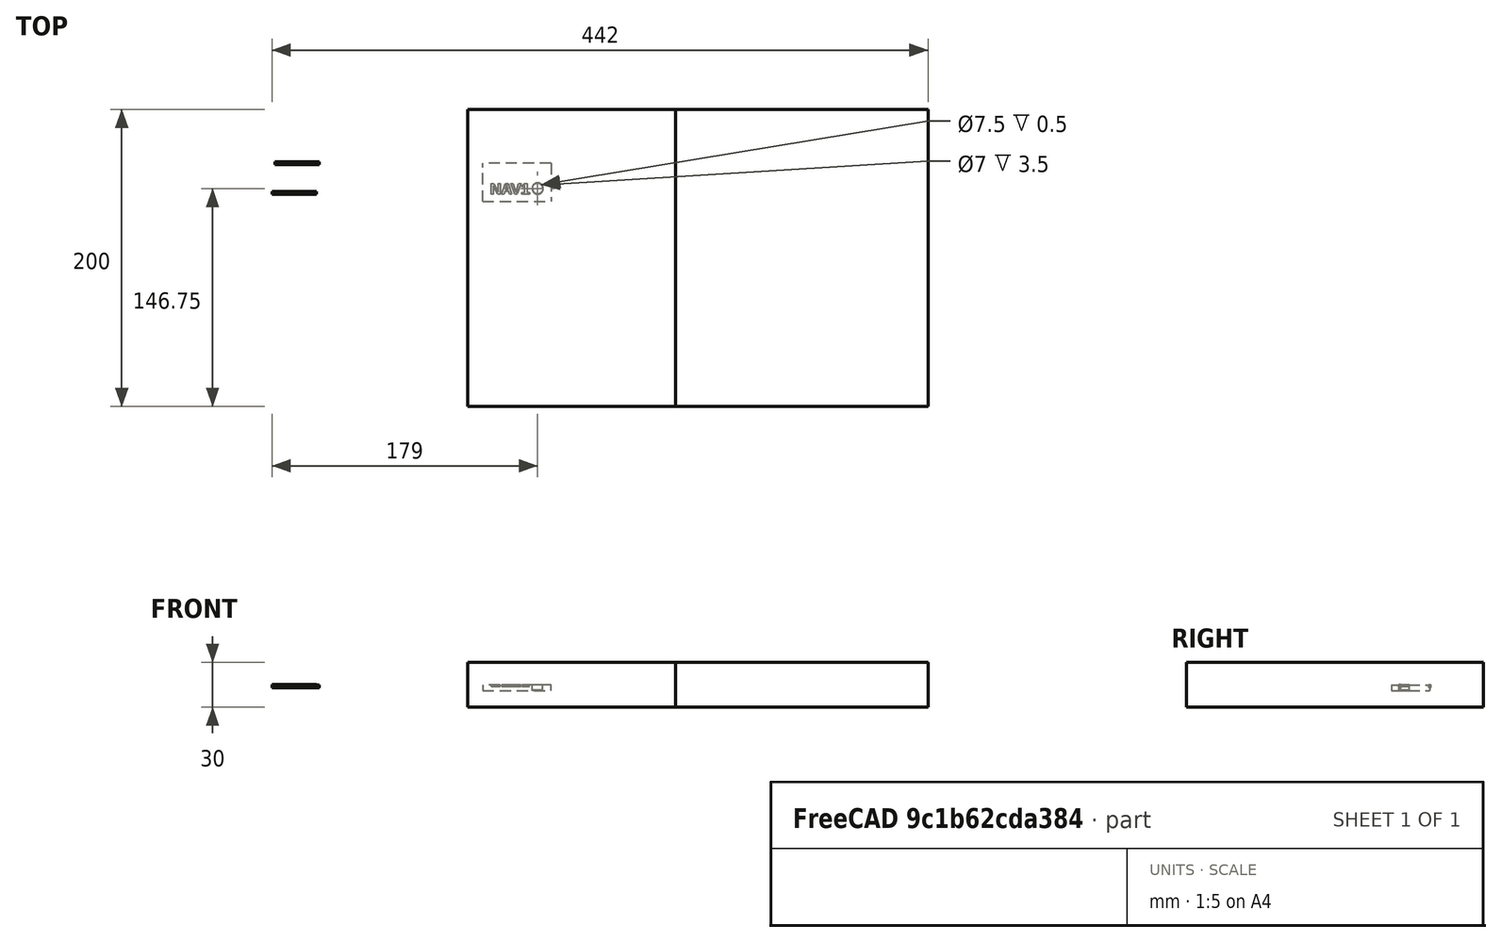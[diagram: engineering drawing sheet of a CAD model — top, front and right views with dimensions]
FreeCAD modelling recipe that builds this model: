
FCSTD DOCUMENT  (FreeCAD 0.17R13522 (Git))
Label: letras_led_1
License: CreativeCommons Attribution-ShareAlike
LicenseURL: http://creativecommons.org/licenses/by-sa/4.0/
objects: Part::Cut×35, Part::Feature×29, Part::Box×10, Part::Part2DObjectPython×7, Part::Fuse×7, Part::Cylinder×5, App::DocumentObjectGroup×3, Part::Extrusion×1
note: 94 computed .brp shape members not serialized (recipe doc carries the construction recipe); baked Part::Feature solids carry a one-line shape summary decoded from their .brp

FEATURE [Part::Part2DObjectPython] Line009  # Draft 2D object (typed FeaturePython)
  ChamferSize = 0
  Closed = false
  End = (270.847,20.2,0)
  FilletRadius = 0
  Length = 35.3471
  MakeFace = false
  Points = (2) [(235.5,20.2,0),(270.847,20.2,0)]
  Start = (235.5,20.2,0)
  Subdivisions = 0
FEATURE [Part::Part2DObjectPython] Circle001  # Draft 2D object (typed FeaturePython)
  FirstAngle = 0
  LastAngle = 0
  MakeFace = false
  Placement = pos=(259.67,20.2,0) rot=(0,0,1;0rad)
  Radius = 14
FEATURE [Part::Part2DObjectPython] Line014  # Draft 2D object (typed FeaturePython)
  ChamferSize = 0
  Closed = false
  End = (248.272,28.2144,0)
  FilletRadius = 0
  Length = 13.696
  MakeFace = false
  Placement = pos=(-10,0,-4) rot=(0,0,1;0rad)
  Points = (2) [(269.378,20.2,4),(258.272,28.2144,4)]
  Start = (259.378,20.2,0)
  Subdivisions = 0
FEATURE [Part::Part2DObjectPython] Line015  # Draft 2D object (typed FeaturePython)
  ChamferSize = 0
  Closed = false
  End = (254.876,33.263,0)
  FilletRadius = 0
  Length = 13.7518
  MakeFace = false
  Placement = pos=(-10,0,-4) rot=(0,0,1;0rad)
  Points = (2) [(269.174,20.2,4),(264.876,33.263,4)]
  Start = (259.174,20.2,0)
  Subdivisions = 0
FEATURE [Part::Part2DObjectPython] Line016  # Draft 2D object (typed FeaturePython)
  ChamferSize = 0
  Closed = false
  End = (263.227,33.6931,0)
  FilletRadius = 0
  Length = 14.1488
  MakeFace = false
  Placement = pos=(-10,0,-4) rot=(0,0,1;0rad)
  Points = (2) [(268.97,20.2,4),(273.227,33.6931,4)]
  Start = (258.97,20.2,0)
  Subdivisions = 0
FEATURE [Part::Part2DObjectPython] Line017  # Draft 2D object (typed FeaturePython)
  ChamferSize = 0
  Closed = false
  End = (270.612,28.9289,0)
  FilletRadius = 0
  Length = 14.5511
  MakeFace = false
  Placement = pos=(-10,0,-4) rot=(0,0,1;0rad)
  Points = (2) [(268.97,20.2,4),(280.612,28.9289,4)]
  Start = (258.97,20.2,0)
  Subdivisions = 0
FEATURE [App::DocumentObjectGroup] Construction
  Group = -> [Line009,Circle001,Line014,Line015,Line016,Line017]
FEATURE [Part::Box] Box001  label="Cube"
  AttacherType = Attacher::AttachEngine3D
  Height = 3
  Length = 6
  Placement = pos=(39,81,-108) rot=(0,0,1;0rad)
  Width = 6
FEATURE [Part::Feature] Fusion008001001061001  label="panel_siplays_encoders_dobles_y_spacers"
  Placement = pos=(0,0,-105) rot=(0,0,1;0rad)
  shape: bbox 280 x 210 x 10 mm, 411 faces (baked)
FEATURE [Part::Feature] Fusion003002001  label="el perforador001"
  Placement = pos=(48,115,-108) rot=(0,1,0;3.14159rad)
  shape: bbox 22 x 12 x 18 mm, 19 faces (baked)
FEATURE [Part::Feature] Fusion003002001001  label="el perforador002"
  Placement = pos=(87.5,115,-108) rot=(0,1,0;3.14159rad)
  shape: bbox 22 x 12 x 18 mm, 19 faces (baked)
FEATURE [Part::Cut] Cut001001001002003001008002002004
  Base = -> Fusion008001001061001
  Refine = true
  Tool = -> Fusion003002001
FEATURE [Part::Feature] Fusion003002001001001  label="el perforador003"
  Placement = pos=(127,115,-108) rot=(0,1,0;3.14159rad)
  shape: bbox 22 x 12 x 18 mm, 19 faces (baked)
FEATURE [Part::Cut] Cut001001001002003001008002002005
  Base = -> Cut001001001002003001008002002004
  Refine = true
  Tool = -> Fusion003002001001
FEATURE [Part::Feature] Fusion003002001001001001  label="el perforador004"
  Placement = pos=(166.5,115,-108) rot=(0,1,0;3.14159rad)
  shape: bbox 22 x 12 x 18 mm, 19 faces (baked)
FEATURE [Part::Feature] Fusion003002001001001001001  label="el perforador005"
  Placement = pos=(206,115,-108) rot=(0,1,0;3.14159rad)
  shape: bbox 22 x 12 x 18 mm, 19 faces (baked)
FEATURE [Part::Cut] Cut001001001002003001008002002006
  Base = -> Cut001001001002003001008002002005
  Refine = true
  Tool = -> Fusion003002001001001001
FEATURE [Part::Cut] Cut001001001002003001008002002007
  Base = -> Cut001001001002003001008002002006
  Refine = true
  Tool = -> Fusion003002001001001001001
FEATURE [Part::Feature] Fusion003002001001001001002001001  label="el perforador008"
  Placement = pos=(127,40,-108) rot=(0,1,0;3.14159rad)
  shape: bbox 22 x 12 x 18 mm, 19 faces (baked)
FEATURE [Part::Feature] Fusion003002001001001001002001002  label="el perforador009"
  Placement = pos=(127,80.5,-108) rot=(0,1,0;3.14159rad)
  shape: bbox 22 x 12 x 18 mm, 19 faces (baked)
FEATURE [Part::Feature] Fusion003002001001001001002001  label="el perforador007"
  Placement = pos=(127,55,-108) rot=(0,1,0;3.14159rad)
  shape: bbox 22 x 12 x 18 mm, 19 faces (baked)
FEATURE [Part::Feature] Fusion003002001001001001002  label="el perforador006"
  Placement = pos=(127,95.5,-108) rot=(0,1,0;3.14159rad)
  shape: bbox 22 x 12 x 18 mm, 19 faces (baked)
FEATURE [Part::Cut] Cut001001001002003001008002002008
  Base = -> Cut001001001002003001008002002007
  Refine = true
  Tool = -> Fusion003002001001001
FEATURE [Part::Cut] Cut001001001002003001008002002009
  Base = -> Cut001001001002003001008002002008
  Refine = true
  Tool = -> Fusion003002001001001001002
FEATURE [Part::Cut] Cut001001001002003001008002002010
  Base = -> Cut001001001002003001008002002009
  Refine = true
  Tool = -> Fusion003002001001001001002001
FEATURE [Part::Box] Box001001002002002001003001001004001001001001001001002  label="Cube034"
  AttacherType = Attacher::AttachEngine3D
  Height = 4
  Length = 32
  Placement = pos=(200,15,-108) rot=(0,0,1;0rad)
  Width = 10
FEATURE [Part::Fuse] Fusion003002001001001001002001003
  Base = -> Cut001001001002003001008002002010
  Refine = true
  Tool = -> Box001001002002002001003001001004001001001001001001002
FEATURE [Part::Fuse] Fusion003002001001001001002001004
  Base = -> Box001001002002002001003001001004001001001001001001002
  Refine = true
  Tool = -> Fusion003002001001001001002001003
FEATURE [Part::Fuse] Fusion003002001001001001002001005
  Refine = true
  Tool = -> Fusion003002001001001001002001004
FEATURE [Part::Fuse] Fusion003002001001001001002001006
  Base = -> Box001
  Refine = true
  Tool = -> Fusion003002001001001001002001005
FEATURE [Part::Feature] Fusion003002001001001001002001002001  label="el perforador010"
  Placement = pos=(47,80.5,-108) rot=(0,1,0;3.14159rad)
  shape: bbox 22 x 12 x 18 mm, 19 faces (baked)
FEATURE [Part::Feature] Fusion003002001001001001002001002002  label="el perforador011"
  Placement = pos=(87,80.5,-108) rot=(0,1,0;3.14159rad)
  shape: bbox 22 x 12 x 18 mm, 19 faces (baked)
FEATURE [Part::Feature] Fusion003002001001001001002001001001  label="el perforador012"
  Placement = pos=(87,40,-108) rot=(0,1,0;3.14159rad)
  shape: bbox 22 x 12 x 18 mm, 19 faces (baked)
FEATURE [Part::Feature] Fusion003002001001001001002001001001001  label="el perforador013"
  Placement = pos=(47,40,-108) rot=(0,1,0;3.14159rad)
  shape: bbox 22 x 12 x 18 mm, 19 faces (baked)
FEATURE [Part::Cut] Cut001001001002003001008002002011
  Base = -> Fusion003002001001001001002001006
  Refine = true
  Tool = -> Fusion003002001001001001002001002
FEATURE [Part::Cut] Cut001001001002003001008002002012
  Base = -> Cut001001001002003001008002002011
  Refine = true
  Tool = -> Fusion003002001001001001002001002002
FEATURE [Part::Cut] Cut001001001002003001008002002013
  Base = -> Cut001001001002003001008002002012
  Refine = true
  Tool = -> Fusion003002001001001001002001002001
FEATURE [Part::Cut] Cut001001001002003001008002002014
  Base = -> Cut001001001002003001008002002013
  Refine = true
  Tool = -> Fusion003002001001001001002001001001001
FEATURE [Part::Feature] Fusion003002001001001001002001001001002  label="el perforador014"
  Placement = pos=(220,8,-108) rot=(0.707107,0.707107,0;3.14159rad)
  shape: bbox 12 x 22 x 18 mm, 19 faces (baked)
FEATURE [Part::Cut] Cut001001001002003001008002002015
  Base = -> Cut001001001002003001008002002014
  Refine = true
  Tool = -> Fusion003002001001001001002001001001
FEATURE [Part::Cut] Cut001001001002003001008002002016
  Base = -> Cut001001001002003001008002002015
  Refine = true
  Tool = -> Fusion003002001001001001002001001
FEATURE [Part::Cut] Cut001001001002003001008002002017  label="base solo faltan los leds"
  Base = -> Cut001001001002003001008002002016
  Refine = true
  Tool = -> Fusion003002001001001001002001001001002
FEATURE [Part::Feature] Fusion001001  label="perforador led 3 mm001 rojo com2"
  Placement = pos=(24,43,-108) rot=(0,1,0;3.14159rad)
  shape: bbox 6 x 6 x 10 mm, 13 faces (baked)
FEATURE [Part::Feature] Fusion003002001001001001002001001001003  label="perforador led 3 mm002 rojo nav2"
  Placement = pos=(61,43,-108) rot=(0,1,0;3.14159rad)
  shape: bbox 6 x 6 x 10 mm, 13 faces (baked)
FEATURE [Part::Feature] Fusion003002001001001001002001001001004  label="perforador led 3 mm002 rojo adf2"
  Placement = pos=(101,43,-108) rot=(0,1,0;3.14159rad)
  shape: bbox 6 x 6 x 10 mm, 13 faces (baked)
FEATURE [Part::Feature] Fusion003002001001001001002001001001005  label="perforador led 3 mm001 rojo com1"
  Placement = pos=(24,83.5,-108) rot=(0,1,0;3.14159rad)
  shape: bbox 6 x 6 x 10 mm, 13 faces (baked)
FEATURE [Part::Feature] Fusion003002001001001001002001001001006  label="perforador led 3 mm002 rojo nav1"
  Placement = pos=(61,83.5,-108) rot=(0,1,0;3.14159rad)
  shape: bbox 6 x 6 x 10 mm, 13 faces (baked)
FEATURE [Part::Feature] Fusion003002001001001001002001001001007  label="perforador led 3 mm002 rojo adf1"
  Placement = pos=(101,83.5,-108) rot=(0,1,0;3.14159rad)
  shape: bbox 6 x 6 x 10 mm, 13 faces (baked)
FEATURE [Part::Cut] Cut
  Base = -> Cut001001001002003001008002002017
  Refine = true
  Tool = -> Fusion003002001001001001002001001001005
FEATURE [Part::Cut] Cut001001001002003001008002002018
  Base = -> Cut
  Refine = true
  Tool = -> Fusion003002001001001001002001001001006
FEATURE [Part::Cut] Cut001001001002003001008002002019
  Base = -> Cut001001001002003001008002002018
  Refine = true
  Tool = -> Fusion003002001001001001002001001001007
FEATURE [Part::Cut] Cut001001001002003001008002002020
  Base = -> Cut001001001002003001008002002019
  Refine = true
  Tool = -> Fusion003002001001001001002001001001004
FEATURE [Part::Cut] Cut001001001002003001008002002021
  Base = -> Cut001001001002003001008002002020
  Refine = true
  Tool = -> Fusion003002001001001001002001001001003
FEATURE [Part::Cut] Cut001001001002003001008002002022
  Base = -> Cut001001001002003001008002002021
  Refine = true
  Tool = -> Fusion001001
FEATURE [Part::Feature] Fusion003002001001001001002001001001008  label="perforador led 5 mm sound marker"
  Placement = pos=(40.75,133,-108) rot=(0,1,0;3.14159rad)
  shape: bbox 7.5 x 7.5 x 10 mm, 13 faces (baked)
FEATURE [Part::Feature] Fusion003002001001001001002001001001009  label="perforador led 5 mm sound com1"
  Placement = pos=(80.25,133,-108) rot=(0,1,0;3.14159rad)
  shape: bbox 7.5 x 7.5 x 10 mm, 13 faces (baked)
FEATURE [Part::Feature] Fusion003002001001001001002001001001010  label="perforador led 5 mm sound nav1"
  Placement = pos=(119.75,133,-108) rot=(0,1,0;3.14159rad)
  shape: bbox 7.5 x 7.5 x 10 mm, 13 faces (baked)
FEATURE [Part::Feature] Fusion003002001001001001002001001001011  label="perforador led 5 mm sound dme"
  Placement = pos=(159.25,133,-108) rot=(0,1,0;3.14159rad)
  shape: bbox 7.5 x 7.5 x 10 mm, 13 faces (baked)
FEATURE [Part::Feature] Fusion003002001001001001002001001001012  label="perforador led 5 mm sound adf1"
  Placement = pos=(198.75,133,-108) rot=(0,1,0;3.14159rad)
  shape: bbox 7.5 x 7.5 x 10 mm, 13 faces (baked)
FEATURE [Part::Feature] Fusion003002001001001001002001001001013  label="perforador led 5 mm ON/OFF"
  Placement = pos=(263.5,133,-108) rot=(0,1,0;3.14159rad)
  shape: bbox 7.5 x 7.5 x 10 mm, 13 faces (baked)
FEATURE [Part::Cut] Cut001001001002003001008002002023
  Base = -> Cut001001001002003001008002002022
  Refine = true
  Tool = -> Fusion003002001001001001002001001001013
FEATURE [Part::Cut] Cut001001001002003001008002002024
  Base = -> Cut001001001002003001008002002023
  Refine = true
  Tool = -> Fusion003002001001001001002001001001012
FEATURE [Part::Cut] Cut001001001002003001008002002025
  Base = -> Cut001001001002003001008002002024
  Refine = true
  Tool = -> Fusion003002001001001001002001001001011
FEATURE [Part::Cut] Cut001001001002003001008002002026
  Base = -> Cut001001001002003001008002002025
  Refine = true
  Tool = -> Fusion003002001001001001002001001001010
FEATURE [Part::Cut] Cut001001001002003001008002002027
  Base = -> Cut001001001002003001008002002026
  Refine = true
  Tool = -> Fusion003002001001001001002001001001009
FEATURE [Part::Cut] Cut001001001002003001008002002028
  Base = -> Cut001001001002003001008002002027
  Refine = true
  Tool = -> Fusion003002001001001001002001001001008
FEATURE [Part::Box] Box  label="Cube035"
  AttacherType = Attacher::AttachEngine3D
  Height = 10
  Length = 300
  Placement = pos=(-8,153.85,-111) rot=(0,0,1;0rad)
  Width = 120
FEATURE [Part::Cut] Cut001001001002003001008002002029  label="panel sin letras"
  Base = -> Cut001001001002003001008002002028
  Refine = true
  Tool = -> Box
FEATURE [Part::Box] Box001001002002002001003001001004001001001001001001003  label="cortador saca parte izquierda"
  AttacherType = Attacher::AttachEngine3D
  Height = 30
  Length = 140
  Placement = pos=(-10,-10,-119) rot=(0,0,1;0rad)
  Width = 200
FEATURE [Part::Box] Box001001002002002001003001001004001001001001001001004  label="cortador saca parte derecha"
  AttacherType = Attacher::AttachEngine3D
  Height = 30
  Length = 170
  Placement = pos=(130,-10,-119) rot=(0,0,1;0rad)
  Width = 200
FEATURE [Part::Cylinder] Cylinder  label="clavija agujereadora1_1"
  Angle = 360
  AttacherType = Attacher::AttachEngine3D
  Height = 30
  Placement = pos=(115,111.85,-106) rot=(0,1,0;1.5708rad)
  Radius = 1.05
FEATURE [Part::Cylinder] Cylinder001  label="clavija agujereadora2_1"
  Angle = 360
  AttacherType = Attacher::AttachEngine3D
  Height = 30
  Placement = pos=(115,37.85,-106) rot=(0,1,0;1.5708rad)
  Radius = 1.05
FEATURE [Part::Cylinder] Cylinder002  label="clavija empalmadora1"
  Angle = 360
  AttacherType = Attacher::AttachEngine3D
  Height = 29.8
  Placement = pos=(-140,153.85,-105) rot=(0,1,0;1.5708rad)
  Radius = 1
FEATURE [Part::Cut] Cut001001001002003001008002002030
  Base = -> Cut001001001002003001008002002029
  Refine = true
  Tool = -> Cylinder
FEATURE [Part::Cut] Cut001001001002003001008002002031  label="panel sin letras con agujeros clavijas"
  Base = -> Cut001001001002003001008002002030
  Refine = true
  Tool = -> Cylinder001
FEATURE [App::DocumentObjectGroup] Group  label="cortadores principales"
  Group = -> [Box001001002002002001003001001004001001001001001001003,Box001001002002002001003001001004001001001001001001004]
FEATURE [Part::Cylinder] Cylinder003  label="clavija hace agujero"
  Angle = 360
  AttacherType = Attacher::AttachEngine3D
  Height = 30
  Placement = pos=(-142,133.85,-105) rot=(0,1,0;1.5708rad)
  Radius = 1.05
FEATURE [App::DocumentObjectGroup] Group001  label="clavijas"
  Group = -> [Cylinder003,Cylinder002]
FEATURE [Part::Box] Box001001002002002001003001001004001001001001001001006  label="fleje abajo"
  AttacherType = Attacher::AttachEngine3D
  Height = 4
  Length = 280
  Placement = pos=(0,-4,-108) rot=(0,0,1;0rad)
  Width = 4
FEATURE [Part::Fuse] Fusion
  Base = -> Cut001001001002003001008002002031
  Refine = true
  Tool = -> Box001001002002002001003001001004001001001001001001006
FEATURE [Part::Feature] Cylinder002001  label="clavija empalmadora une frente base"
  Placement = pos=(30,-2,-134) rot=(0,0,1;1.5708rad)
  shape: bbox 2 x 2 x 29.8 mm, 3 faces (baked)
FEATURE [Part::Feature] Cylinder002001001  label="clavija empalmadora une frente base2"
  Placement = pos=(250,-2,-134) rot=(0,0,1;1.5708rad)
  shape: bbox 2 x 2 x 29.8 mm, 3 faces (baked)
FEATURE [Part::Fuse] Fusion003002001001001001002001001001014
  Base = -> Fusion
  Refine = true
  Tool = -> Cylinder002001
FEATURE [Part::Fuse] Fusion003002001001001001002001001001015  label="frente con clavijas sin letras"
  Base = -> Cylinder002001001
  Refine = true
  Tool = -> Fusion003002001001001001002001001001014
FEATURE [Part::Box] Box001001002002002001003001001004001001001001001001007  label="cortador clavijas"
  AttacherType = Attacher::AttachEngine3D
  Height = 4
  Length = 280
  Placement = pos=(0,0,-153) rot=(1,0,0;1.5708rad)
  Width = 30
FEATURE [Part::Cut] Cut001001001002003001008002002032  label="frente con clavijas de 15 sin letras"
  Base = -> Fusion003002001001001001002001001001015
  Refine = true
  Tool = -> Box001001002002002001003001001004001001001001001001007
FEATURE [Part::Box] Box001001002002002001003001001004001001001001001001008  label="Cube036"
  AttacherType = Attacher::AttachEngine3D
  Height = 60
  Length = 300
  Placement = pos=(46,-26,-134) rot=(0,0,1;0rad)
  Width = 200
FEATURE [Part::Cut] Cut001001001002003001008002002033
  Base = -> Cut001001001002003001008002002032
  Refine = true
  Tool = -> Box001001002002002001003001001004001001001001001001008
FEATURE [Part::Box] Box001001002002002001003001001004001001001001001001009  label="Cube037"
  AttacherType = Attacher::AttachEngine3D
  Height = 60
  Length = 100
  Placement = pos=(-22,-23,-132) rot=(0,0,1;0rad)
  Width = 100
FEATURE [Part::Cut] Cut001001001002003001008002002034
  Base = -> Cut001001001002003001008002002033
  Refine = true
  Tool = -> Box001001002002002001003001001004001001001001001001009
FEATURE [Part::Part2DObjectPython] ShapeString  # Draft 2D object (typed FeaturePython)
  FontFile = <path>
  Placement = pos=(4.96,132.99,-104) rot=(0,0,1;0rad)
  Size = 8
  String = NAV1
  Tracking = 0
FEATURE [Part::Extrusion] Extrude
  Base = -> ShapeString
  Dir = (0,0,1)
  DirMode = 2
  FaceMakerClass = Part::FaceMakerBullseye
  LengthFwd = 1
  LengthRev = 0
  Placement = pos=(0,0,-1) rot=(0,0,1;0rad)
  Solid = false
  Symmetric = false
FEATURE [Part::Cut] Cut001001001002003001008002002035
  Base = -> Cut001001001002003001008002002034
  Refine = true
  Tool = -> Extrude
FEATURE [Part::Box] Box001001002002002001003001001004001001001001001001010  label="Cube038"
  AttacherType = Attacher::AttachEngine3D
  Height = 60
  Length = 100
  Placement = pos=(-16,28,-120) rot=(0,0,1;0rad)
  Width = 100
FEATURE [Part::Cut] Cut001001001002003001008002002036
  Base = -> Cut001001001002003001008002002035
  Refine = true
  Tool = -> Box001001002002002001003001001004001001001001001001010
FEATURE [Part::Cylinder] Cylinder002001002  label="Cylinder"
  Angle = 360
  AttacherType = Attacher::AttachEngine3D
  Height = 38
  Placement = pos=(37,136.75,-132) rot=(0,0,1;0rad)
  Radius = 3.5
FEATURE [Part::Cut] Cut001001001002003001008002002037
  Base = -> Cut001001001002003001008002002036
  Refine = true
  Tool = -> Cylinder002001002
note: 1 file-system path scrubbed to <path> (originals preserved in the JSON sidecar)
